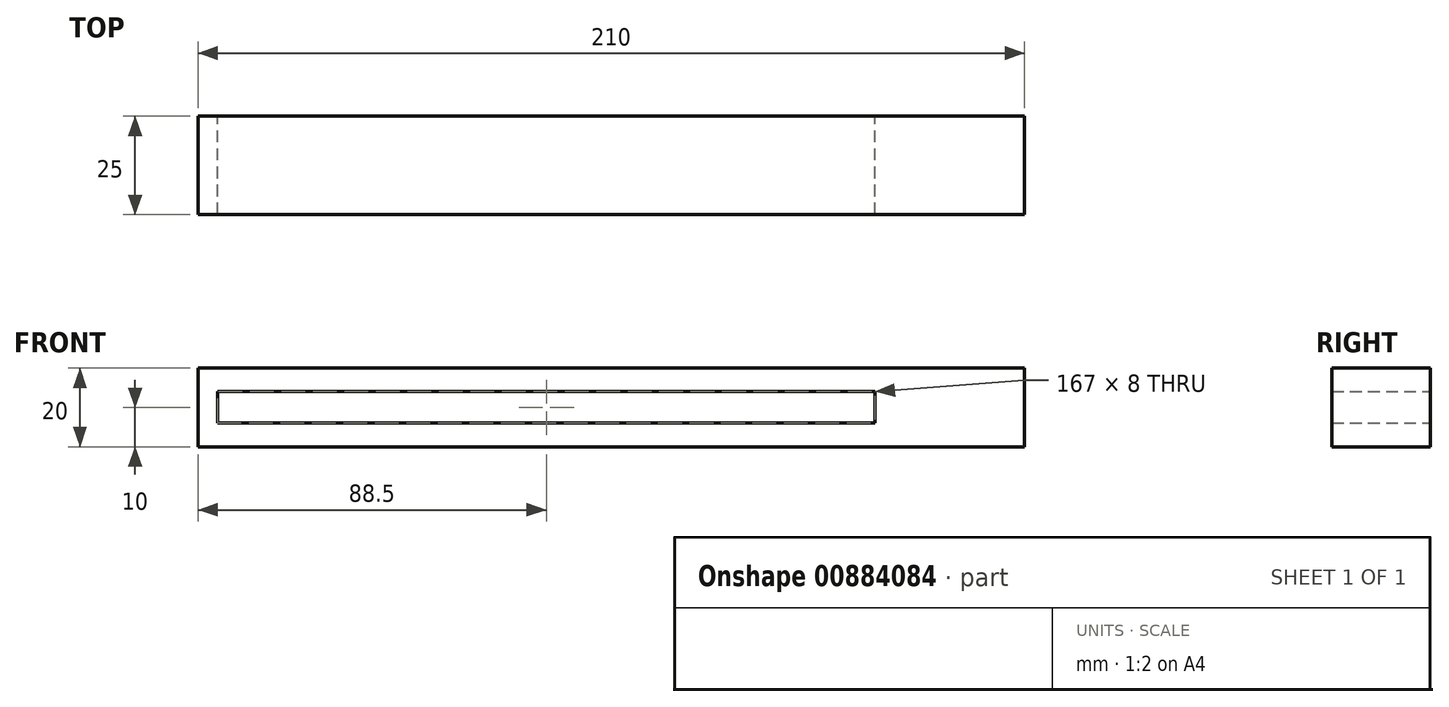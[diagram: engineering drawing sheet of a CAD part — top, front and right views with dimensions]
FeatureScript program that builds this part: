
annotation { "Feature Type Name" : "Feature", "Feature Type Description" : "" }
export const myFeature = defineFeature(function(context is Context, id is Id, definition is map)
    precondition{}
    {
        {
            var Q0;
            Q0=qCreatedBy(makeId("Front.planeOp"),FACE);
            var sketch = newSketch(context, id + "F0", { "sketchPlane" : qUnion([Q0])});
            skLineSegment(sketch, "E0.bottom", {"start": v(0, 0) * mm, "end": v(210, 0) * mm});
            skLineSegment(sketch, "E0.top", {"start": v(0, 20) * mm, "end": v(210, 20) * mm});
            skLineSegment(sketch, "E0.left", {"start": v(0, 0) * mm, "end": v(0, 20) * mm});
            skLineSegment(sketch, "E0.right", {"start": v(210, 0) * mm, "end": v(210, 20) * mm});
            skPoint(sketch, "E1", {"position": v(5, 0) * mm});
            skPoint(sketch, "E2", {"position": v(0, 6) * mm});
            skPoint(sketch, "E3", {"position": v(0, 14) * mm});
            skLineSegment(sketch, "E4.bottom", {"start": v(5, 6) * mm, "end": v(172, 6) * mm});
            skLineSegment(sketch, "E4.top", {"start": v(5, 14) * mm, "end": v(172, 14) * mm});
            skLineSegment(sketch, "E4.left", {"start": v(5, 6) * mm, "end": v(5, 14) * mm});
            skLineSegment(sketch, "E4.right", {"start": v(172, 6) * mm, "end": v(172, 14) * mm});
            skSolve(sketch);
        }
        {
            var Q0;
            Q0=makeQuery(id+"F0.imprint","IMPRINT",FACE,{"disambiguationData":[TD([[makeQuery(id+"F0.imprint","IMPRINT",EDGE,{"derivedFrom":sQuery(id+"F0.wireOp",EDGE,"E4.bottom")}),1.0]])]});
            extrude(context, id + "F1", {"entities" : qUnion([Q0]), "depth" : 25 * mm, "offsetDistance" : 25 * mm});
        }
        {
            var Q0;
            Q0=makeQuery(id+"F0.imprint","IMPRINT",FACE,{"disambiguationData":[TD([[makeQuery(id+"F0.imprint","IMPRINT",EDGE,{"derivedFrom":sQuery(id+"F0.wireOp",EDGE,"E0.bottom")}),1.0]])]});
            extrude(context, id + "F2", {"entities" : qUnion([Q0]), "depth" : 25 * mm, "offsetDistance" : 25 * mm});
        }
    });
